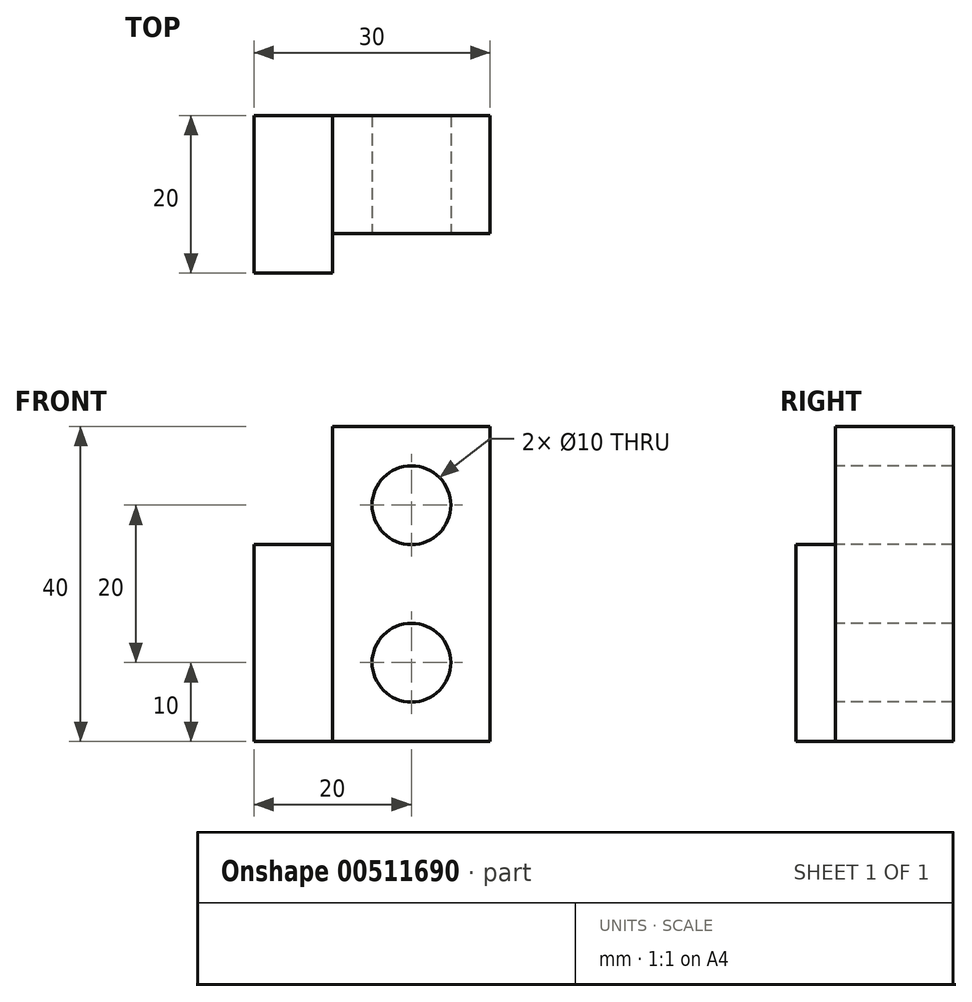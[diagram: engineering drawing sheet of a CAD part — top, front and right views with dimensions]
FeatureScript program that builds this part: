
annotation { "Feature Type Name" : "Feature", "Feature Type Description" : "" }
export const myFeature = defineFeature(function(context is Context, id is Id, definition is map)
    precondition{}
    {
        {
            var Q0;
            Q0=qCreatedBy(makeId("Front.planeOp"),FACE);
            var sketch = newSketch(context, id + "F0", { "sketchPlane" : qUnion([Q0])});
            skLineSegment(sketch, "E0.bottom", {"start": v(-10, 20) * mm, "end": v(10, 20) * mm});
            skLineSegment(sketch, "E0.top", {"start": v(-10, -20) * mm, "end": v(10, -20) * mm});
            skLineSegment(sketch, "E0.left", {"start": v(-10, 20) * mm, "end": v(-10, -20) * mm});
            skLineSegment(sketch, "E0.right", {"start": v(10, 20) * mm, "end": v(10, -20) * mm});
            skPoint(sketch, "E0.middle", {"position": v(0, 0) * mm});
            skSolve(sketch);
        }
        {
            var Q0;
            Q0 = qSketchRegion(id + "F0", true);
            extrude(context, id + "F1", {"entities" : qUnion([Q0]), "depth" : 15 * mm, "offsetDistance" : 25.4 * mm});
        }
        {
            var Q0;
            Q0=makeQuery(id+"F1.opExtrude","CAP_FACE",FACE,{"disambiguationData":[OSD([sQuery(id+"F0.wireOp",EDGE,"E0.bottom"),sQuery(id+"F0.wireOp",EDGE,"E0.top"),sQuery(id+"F0.wireOp",EDGE,"E0.left"),sQuery(id+"F0.wireOp",EDGE,"E0.right")])],"isStart":false});
            var sketch = newSketch(context, id + "F2", { "sketchPlane" : qUnion([Q0])});
            skPoint(sketch, "E1", {"position": v(0, 10) * mm});
            skPoint(sketch, "E2", {"position": v(0, -10) * mm});
            skPoint(sketch, "E3", {"position": v(0, 20) * mm});
            skPoint(sketch, "E4", {"position": v(0, -20) * mm});
            skSolve(sketch);
        }
        {
            var Q0;
            Q0=sQuery(id+"F2.wireOp",VERTEX,"E1");
            var Q1;
            Q1=sQuery(id+"F2.wireOp",VERTEX,"E2");
            var Q2;
            Q2=makeQuery(id+"F1.opExtrude","SWEPT_BODY",BODY,{"disambiguationData":[OSD([sQuery(id+"F0.wireOp",EDGE,"E0.bottom"),sQuery(id+"F0.wireOp",EDGE,"E0.top"),sQuery(id+"F0.wireOp",EDGE,"E0.left"),sQuery(id+"F0.wireOp",EDGE,"E0.right")])]});
            hole(context, id + "F3", {"style" : HoleStyle.SIMPLE, "endStyle" : HoleEndStyle.BLIND, "holeDiameter" : 10 * mm, "majorDiameter" : 6.35 * mm, "holeDepth" : 25.4 * mm, "isTappedThrough" : true, "tappedDepth" : 12.7 * mm, "tapClearance" : 3, "locations" : qUnion([Q0, Q1]), "scope" : qUnion([Q2])});
        }
        {
            var Q0;
            Q0=makeQuery(id+"F1.opExtrude","SWEPT_FACE",FACE,{"disambiguationData":[OSD([sQuery(id+"F0.wireOp",EDGE,"E0.left")])]});
            var sketch = newSketch(context, id + "F4", { "sketchPlane" : qUnion([Q0])});
            skLineSegment(sketch, "E5.bottom", {"start": v(0, -20) * mm, "end": v(20, -20) * mm});
            skLineSegment(sketch, "E5.top", {"start": v(0, 5) * mm, "end": v(20, 5) * mm});
            skLineSegment(sketch, "E5.left", {"start": v(0, -20) * mm, "end": v(0, 5) * mm});
            skLineSegment(sketch, "E5.right", {"start": v(20, -20) * mm, "end": v(20, 5) * mm});
            skSolve(sketch);
        }
        {
            var Q0;
            Q0 = qSketchRegion(id + "F4", true);
            extrude(context, id + "F5", {"entities" : qUnion([Q0]), "operationType" : NewBodyOperationType.ADD, "depth" : 10 * mm, "offsetDistance" : 25.4 * mm});
        }
    });
